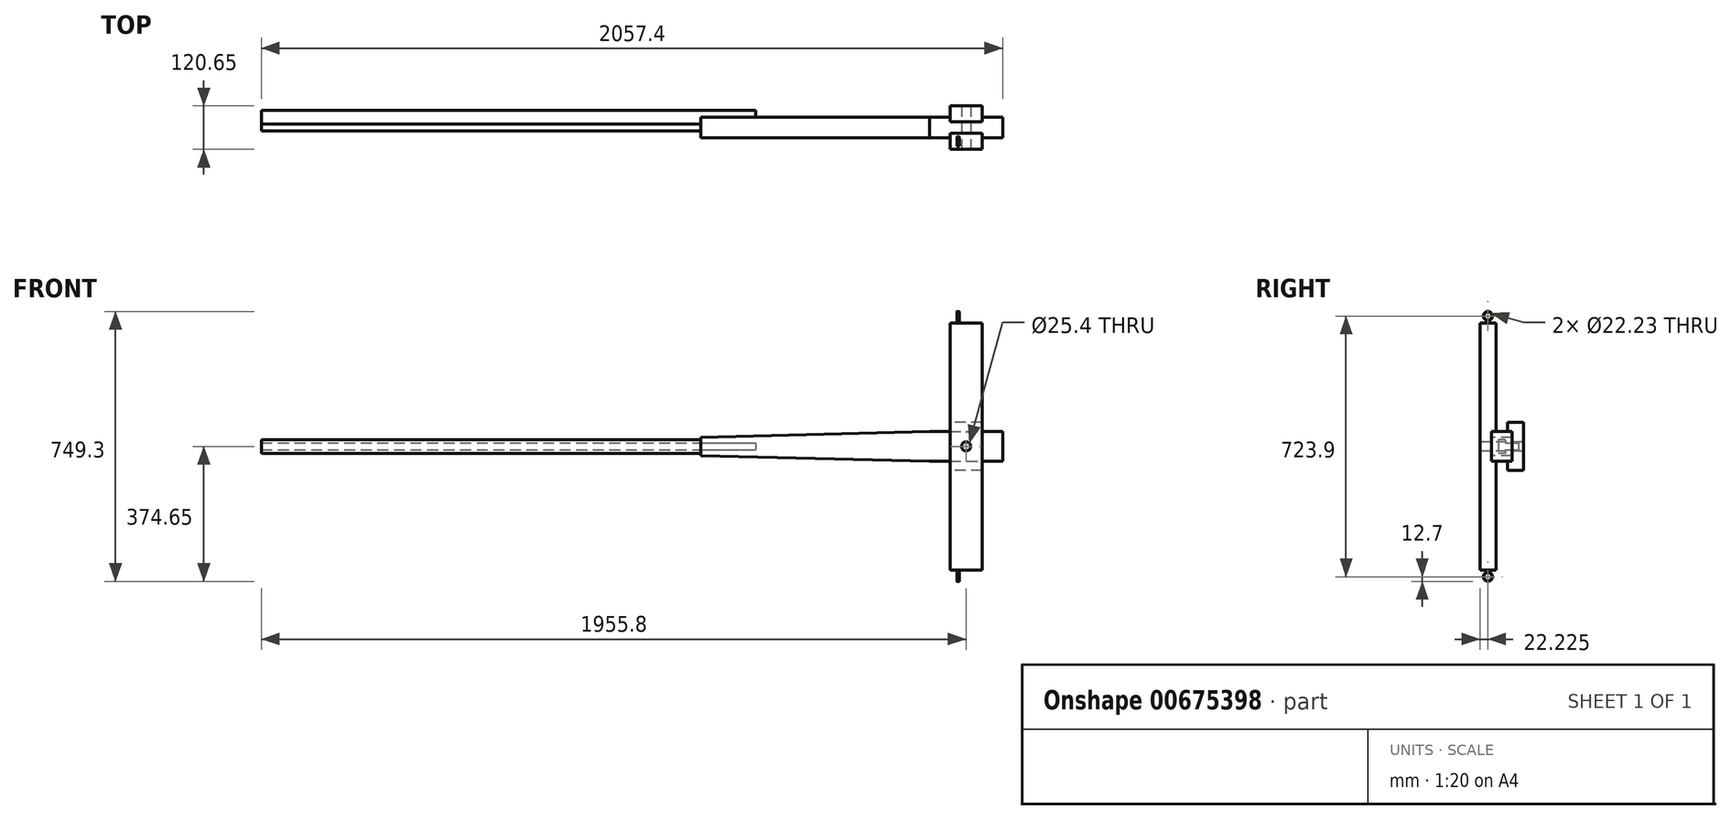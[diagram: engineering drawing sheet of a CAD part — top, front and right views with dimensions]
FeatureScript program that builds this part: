
annotation { "Feature Type Name" : "Feature", "Feature Type Description" : "" }
export const myFeature = defineFeature(function(context is Context, id is Id, definition is map)
    precondition{}
    {
        {
            var Q0;
            Q0=qCreatedBy(makeId("Front.planeOp"),FACE);
            var sketch = newSketch(context, id + "F0", { "sketchPlane" : qUnion([Q0])});
            skLineSegment(sketch, "E0.bottom", {"start": v(101.6, 41.27) * mm, "end": v(-736.6, 41.27) * mm});
            skLineSegment(sketch, "E0.top", {"start": v(101.6, -41.27) * mm, "end": v(-736.6, -41.28) * mm});
            skLineSegment(sketch, "E0.left", {"start": v(101.6, 41.28) * mm, "end": v(101.6, -41.27) * mm});
            skLineSegment(sketch, "E0.right", {"start": v(-736.6, 41.27) * mm, "end": v(-736.6, -41.28) * mm});
            skSolve(sketch);
        }
        {
            var Q0;
            Q0=qSketchRegion(id+"F0",true);
            extrude(context, id + "F1", {"entities" : qUnion([Q0]), "depth" : 57.15 * mm, "offsetDistance" : 25.4 * mm});
        }
        {
            var Q0;
            Q0=makeQuery(id+"F1.opExtrude","CAP_FACE",FACE,{"disambiguationData":[OSD([sQuery(id+"F0.wireOp",EDGE,"E0.bottom"),sQuery(id+"F0.wireOp",EDGE,"E0.top"),sQuery(id+"F0.wireOp",EDGE,"E0.left"),sQuery(id+"F0.wireOp",EDGE,"E0.right")])],"isStart":false});
            var sketch = newSketch(context, id + "F2", { "sketchPlane" : qUnion([Q0])});
            skLineSegment(sketch, "E1", {"start": v(-736.6, 41.27) * mm, "end": v(-736.6, 25.4) * mm});
            skLineSegment(sketch, "E2", {"start": v(-736.6, 25.4) * mm, "end": v(-101.6, 41.27) * mm});
            skLineSegment(sketch, "E3", {"start": v(-101.6, 41.27) * mm, "end": v(-736.6, 41.27) * mm});
            skLineSegment(sketch, "E4", {"start": v(-736.6, -41.28) * mm, "end": v(-736.6, -25.4) * mm});
            skLineSegment(sketch, "E5", {"start": v(-736.6, -25.4) * mm, "end": v(-101.6, -41.27) * mm});
            skLineSegment(sketch, "E6", {"start": v(-101.6, -41.28) * mm, "end": v(-736.6, -41.28) * mm});
            skSolve(sketch);
        }
        {
            var Q0;
            Q0=qSketchRegion(id+"F2",true);
            extrude(context, id + "F3", {"entities" : qUnion([Q0]), "operationType" : NewBodyOperationType.REMOVE, "endBound" : BoundingType.THROUGH_ALL, "oppositeDirection" : true, "depth" : 25.4 * mm, "offsetDistance" : 25.4 * mm});
        }
        {
            var Q0;
            Q0=makeQuery(id+"F1.opExtrude","CAP_FACE",FACE,{"disambiguationData":[OSD([sQuery(id+"F0.wireOp",EDGE,"E0.bottom"),sQuery(id+"F0.wireOp",EDGE,"E0.top"),sQuery(id+"F0.wireOp",EDGE,"E0.left"),sQuery(id+"F0.wireOp",EDGE,"E0.right")])],"isStart":false});
            var sketch = newSketch(context, id + "F4", { "sketchPlane" : qUnion([Q0])});
            skLineSegment(sketch, "E7.left", {"start": v(-44.45, 342.9) * mm, "end": v(-44.45, -342.9) * mm});
            skLineSegment(sketch, "E7.right", {"start": v(44.45, 342.9) * mm, "end": v(44.45, -342.9) * mm});
            skLineSegment(sketch, "E8", {"start": v(-44.45, -342.9) * mm, "end": v(44.45, -342.9) * mm});
            skLineSegment(sketch, "E9", {"start": v(-44.45, 342.9) * mm, "end": v(44.45, 342.9) * mm});
            skSolve(sketch);
        }
        {
            var Q0;
            {var subQ0=sQuery(id+"F4.wireOp",EDGE,"E7.left");var subQ1=makeQuery(id+"F1.opExtrude","CAP_EDGE",EDGE,{"disambiguationData":[OSD([sQuery(id+"F0.wireOp",EDGE,"E0.bottom")])],"isStart":false});var subQ2=makeQuery(id+"F4.imprint","INTERSECT",VERTEX,{"derivedFrom":[subQ1,subQ0]});Q0=makeQuery(id+"F4.imprint","IMPRINT",FACE,{"disambiguationData":[TD([[makeQuery(id+"F4.imprint","IMPRINT",EDGE,{"disambiguationData":[TD([[subQ2,-1.0]])],"derivedFrom":subQ0}),1.0]])]});}
            var Q1;
            {var subQ0=sQuery(id+"F4.wireOp",EDGE,"E9");Q1=makeQuery(id+"F4.imprint","IMPRINT",FACE,{"disambiguationData":[TD([[makeQuery(id+"F4.imprint","IMPRINT",EDGE,{"derivedFrom":subQ0}),-1.0]])]});}
            var Q2;
            {var subQ0=sQuery(id+"F4.wireOp",EDGE,"E8");Q2=makeQuery(id+"F4.imprint","IMPRINT",FACE,{"disambiguationData":[TD([[makeQuery(id+"F4.imprint","IMPRINT",EDGE,{"derivedFrom":subQ0}),1.0]])]});}
            extrude(context, id + "F5", {"entities" : qUnion([Q0, Q1, Q2]), "operationType" : NewBodyOperationType.ADD, "depth" : 31.75 * mm, "offsetDistance" : 25.4 * mm, "hasSecondDirection" : true, "secondDirectionOppositeDirection" : true, "secondDirectionDepth" : 12.7 * mm});
        }
        {
            var Q0;
            Q0=makeQuery(id+"F5.opExtrude","CAP_FACE",FACE,{"disambiguationData":[OSD([sQuery(id+"F4.wireOp",EDGE,"E7.left"),sQuery(id+"F4.wireOp",EDGE,"E7.right"),sQuery(id+"F4.wireOp",EDGE,"c8be6581-7b69-41f4-ac51-68e8a2e033d9.bottom"),sQuery(id+"F4.wireOp",EDGE,"c8be6581-7b69-41f4-ac51-68e8a2e033d9.top"),sQuery(id+"F4.wireOp",EDGE,"c8be6581-7b69-41f4-ac51-68e8a2e033d9.left"),sQuery(id+"F4.wireOp",EDGE,"c8be6581-7b69-41f4-ac51-68e8a2e033d9.right"),sQuery(id+"F4.wireOp",EDGE,"86981ba0-bfa5-46fc-8650-502ccc05c84c.bottom"),sQuery(id+"F4.wireOp",EDGE,"86981ba0-bfa5-46fc-8650-502ccc05c84c.top"),sQuery(id+"F4.wireOp",EDGE,"86981ba0-bfa5-46fc-8650-502ccc05c84c.left"),sQuery(id+"F4.wireOp",EDGE,"86981ba0-bfa5-46fc-8650-502ccc05c84c.right")])],"isStart":false});
            var sketch = newSketch(context, id + "F6", { "sketchPlane" : qUnion([Q0])});
            skCircle(sketch, "E10", {"center": v(0, 0) * mm, "radius": 12.7 * mm});
            skSolve(sketch);
        }
        {
            var Q0;
            Q0=qSketchRegion(id+"F6",true);
            extrude(context, id + "F7", {"entities" : qUnion([Q0]), "operationType" : NewBodyOperationType.REMOVE, "endBound" : BoundingType.THROUGH_ALL, "oppositeDirection" : true, "depth" : 25.4 * mm, "offsetDistance" : 25.4 * mm});
        }
        {
            var Q0;
            Q0=makeQuery(id+"F1.opExtrude","SWEPT_FACE",FACE,{"disambiguationData":[OSD([sQuery(id+"F0.wireOp",EDGE,"E0.right")])]});
            var sketch = newSketch(context, id + "F8", { "sketchPlane" : qUnion([Q0])});
            skLineSegment(sketch, "E11.bottom", {"start": v(19.05, 19.05) * mm, "end": v(38.1, 19.05) * mm});
            skLineSegment(sketch, "E11.top", {"start": v(19.05, -19.05) * mm, "end": v(38.1, -19.05) * mm});
            skLineSegment(sketch, "E11.left", {"start": v(19.05, 19.05) * mm, "end": v(19.05, -19.05) * mm});
            skLineSegment(sketch, "E11.right", {"start": v(38.1, 19.05) * mm, "end": v(38.1, -19.05) * mm});
            skLineSegment(sketch, "E12.left", {"start": v(38.1, 19.05) * mm, "end": v(38.1, 0) * mm});
            skLineSegment(sketch, "E13.left", {"start": v(19.05, -19.05) * mm, "end": v(19.05, 0) * mm});
            skLineSegment(sketch, "E14.bottom", {"start": v(19.05, -9.52) * mm, "end": v(-19.05, -9.52) * mm});
            skLineSegment(sketch, "E14.top", {"start": v(19.05, 9.53) * mm, "end": v(-19.05, 9.53) * mm});
            skLineSegment(sketch, "E14.left", {"start": v(19.05, -9.52) * mm, "end": v(19.05, 9.53) * mm});
            skLineSegment(sketch, "E14.right", {"start": v(-19.05, -9.52) * mm, "end": v(-19.05, 9.53) * mm});
            skSolve(sketch);
        }
        {
            var Q0;
            Q0=qSketchRegion(id+"F8",true);
            extrude(context, id + "F9", {"entities" : qUnion([Q0]), "operationType" : NewBodyOperationType.ADD, "depth" : 1219.2 * mm, "offsetDistance" : 25.4 * mm, "hasSecondDirection" : true, "secondDirectionOppositeDirection" : true, "secondDirectionDepth" : 152.4 * mm});
        }
        {
            var Q0;
            Q0=makeQuery(id+"F1.opExtrude","CAP_FACE",FACE,{"disambiguationData":[OSD([sQuery(id+"F0.wireOp",EDGE,"E0.bottom"),sQuery(id+"F0.wireOp",EDGE,"E0.top"),sQuery(id+"F0.wireOp",EDGE,"E0.left"),sQuery(id+"F0.wireOp",EDGE,"E0.right")])],"isStart":true});
            var sketch = newSketch(context, id + "F10", { "sketchPlane" : qUnion([Q0])});
            skLineSegment(sketch, "E15.bottom", {"start": v(-44.45, 66.67) * mm, "end": v(44.45, 66.67) * mm});
            skLineSegment(sketch, "E15.top", {"start": v(-44.45, -66.68) * mm, "end": v(44.45, -66.68) * mm});
            skLineSegment(sketch, "E15.left", {"start": v(-44.45, 66.67) * mm, "end": v(-44.45, -66.68) * mm});
            skLineSegment(sketch, "E15.right", {"start": v(44.45, 66.67) * mm, "end": v(44.45, -66.68) * mm});
            skSolve(sketch);
        }
        {
            var Q0;
            Q0 = qSketchRegion(id + "F10", true);
            extrude(context, id + "F11", {"entities" : qUnion([Q0]), "operationType" : NewBodyOperationType.ADD, "depth" : 31.75 * mm, "offsetDistance" : 25.4 * mm, "hasSecondDirection" : true, "secondDirectionOppositeDirection" : true, "secondDirectionDepth" : 12.7 * mm});
        }
        {
            var Q0;
            Q0=makeQuery(id+"F11.opExtrude","CAP_FACE",FACE,{"disambiguationData":[OSD([sQuery(id+"F10.wireOp",EDGE,"E15.bottom"),sQuery(id+"F10.wireOp",EDGE,"E15.top"),sQuery(id+"F10.wireOp",EDGE,"E15.left"),sQuery(id+"F10.wireOp",EDGE,"E15.right")])],"isStart":false});
            var sketch = newSketch(context, id + "F12", { "sketchPlane" : qUnion([Q0])});
            skCircle(sketch, "E16", {"center": v(0, 0) * mm, "radius": 12.7 * mm});
            skSolve(sketch);
        }
        {
            var Q0;
            Q0 = qSketchRegion(id + "F12", true);
            extrude(context, id + "F13", {"entities" : qUnion([Q0]), "operationType" : NewBodyOperationType.REMOVE, "endBound" : BoundingType.THROUGH_ALL, "oppositeDirection" : true, "depth" : 25.4 * mm, "offsetDistance" : 25.4 * mm});
        }
        {
            var Q0;
            Q0=makeQuery(id+"F5.opExtrude","SWEPT_FACE",FACE,{"disambiguationData":[OSD([sQuery(id+"F4.wireOp",EDGE,"E7.left")])]});
            var sketch = newSketch(context, id + "F14", { "sketchPlane" : qUnion([Q0])});
            skCircle(sketch, "E17", {"center": v(66.68, 361.95) * mm, "radius": 11.11 * mm});
            skArc(sketch, "E18", {"start": v(69.85, 349.65) * mm, "mid": v(66.67, 374.65) * mm, "end": v(63.5, 349.65) * mm});
            skLineSegment(sketch, "E19.top", {"start": v(63.5, 323.85) * mm, "end": v(69.85, 323.85) * mm});
            skLineSegment(sketch, "E19.left", {"start": v(63.5, 349.65) * mm, "end": v(63.5, 323.85) * mm});
            skLineSegment(sketch, "E19.right", {"start": v(69.85, 349.65) * mm, "end": v(69.85, 323.85) * mm});
            skSolve(sketch);
        }
        {
            var Q0;
            Q0 = qSketchRegion(id + "F14", true);
            extrude(context, id + "F15", {"entities" : qUnion([Q0]), "operationType" : NewBodyOperationType.ADD, "oppositeDirection" : true, "depth" : 25.4 * mm, "offsetDistance" : 25.4 * mm, "hasSecondDirection" : true, "secondDirectionOppositeDirection" : true, "secondDirectionDepth" : 19.05 * mm});
        }
        {
            var Q0;
            Q0=makeQuery(id+"F15.opExtrude","CAP_EDGE",EDGE,{"disambiguationData":[OSD([sQuery(id+"F14.wireOp",EDGE,"E19.right")])],"isStart":true});
            var Q1;
            Q1=makeQuery(id+"F15.opExtrude","CAP_EDGE",EDGE,{"disambiguationData":[OSD([sQuery(id+"F14.wireOp",EDGE,"E19.left")])],"isStart":true});
            var Q2;
            Q2=makeQuery(id+"F15.opExtrude","CAP_EDGE",EDGE,{"disambiguationData":[OSD([sQuery(id+"F14.wireOp",EDGE,"E19.right")])],"isStart":false});
            var Q3;
            Q3=makeQuery(id+"F15.opExtrude","CAP_EDGE",EDGE,{"disambiguationData":[OSD([sQuery(id+"F14.wireOp",EDGE,"E19.left")])],"isStart":false});
            fillet(context, id + "F16", {"entities" : qUnion([Q0, Q1, Q2, Q3]), "radius" : 3.17 * mm, "tangentPropagation" : true, "allowEdgeOverflow" : false});
        }
        {
            var Q0;
            Q0=makeQuery(id+"F15.opExtrude","CAP_EDGE",EDGE,{"disambiguationData":[OSD([sQuery(id+"F14.wireOp",EDGE,"E17")])],"isStart":true});
            var Q1;
            Q1=makeQuery(id+"F15.opExtrude","CAP_EDGE",EDGE,{"disambiguationData":[OSD([sQuery(id+"F14.wireOp",EDGE,"E18")])],"isStart":true});
            var Q2;
            Q2=makeQuery(id+"F15.opExtrude","CAP_EDGE",EDGE,{"disambiguationData":[OSD([sQuery(id+"F14.wireOp",EDGE,"E17")])],"isStart":false});
            var Q3;
            Q3=makeQuery(id+"F15.opExtrude","CAP_EDGE",EDGE,{"disambiguationData":[OSD([sQuery(id+"F14.wireOp",EDGE,"E18")])],"isStart":false});
            fillet(context, id + "F17", {"entities" : qUnion([Q0, Q1, Q2, Q3]), "radius" : 0.64 * mm, "tangentPropagation" : true, "allowEdgeOverflow" : false});
        }
        {
            var Q0;
            Q0=makeQuery(id+"F5.opExtrude","SWEPT_FACE",FACE,{"disambiguationData":[OSD([sQuery(id+"F4.wireOp",EDGE,"E7.left")])]});
            var sketch = newSketch(context, id + "F18", { "sketchPlane" : qUnion([Q0])});
            skArc(sketch, "E20.MirrorCS", {"start": v(69.85, -349.65) * mm, "mid": v(66.67, -374.65) * mm, "end": v(63.5, -349.65) * mm});
            skLineSegment(sketch, "E21.MirrorCS", {"start": v(63.5, -323.85) * mm, "end": v(69.85, -323.85) * mm});
            skLineSegment(sketch, "E22.MirrorCS", {"start": v(63.5, -349.65) * mm, "end": v(63.5, -323.85) * mm});
            skLineSegment(sketch, "E23.MirrorCS", {"start": v(69.85, -349.65) * mm, "end": v(69.85, -323.85) * mm});
            skCircle(sketch, "E24.MirrorC", {"center": v(66.68, -361.95) * mm, "radius": 11.11 * mm});
            skSolve(sketch);
        }
        {
            var Q0;
            Q0 = qSketchRegion(id + "F18", true);
            extrude(context, id + "F19", {"entities" : qUnion([Q0]), "operationType" : NewBodyOperationType.ADD, "oppositeDirection" : true, "depth" : 25.4 * mm, "offsetDistance" : 25.4 * mm, "hasSecondDirection" : true, "secondDirectionOppositeDirection" : true, "secondDirectionDepth" : 19.05 * mm});
        }
        {
            var Q0;
            Q0=makeQuery(id+"F19.opExtrude","CAP_EDGE",EDGE,{"disambiguationData":[OSD([sQuery(id+"F18.wireOp",EDGE,"E23.MirrorCS")])],"isStart":true});
            var Q1;
            Q1=makeQuery(id+"F19.opExtrude","CAP_EDGE",EDGE,{"disambiguationData":[OSD([sQuery(id+"F18.wireOp",EDGE,"E22.MirrorCS")])],"isStart":true});
            var Q2;
            Q2=makeQuery(id+"F19.opExtrude","CAP_EDGE",EDGE,{"disambiguationData":[OSD([sQuery(id+"F18.wireOp",EDGE,"E23.MirrorCS")])],"isStart":false});
            var Q3;
            Q3=makeQuery(id+"F19.opExtrude","CAP_EDGE",EDGE,{"disambiguationData":[OSD([sQuery(id+"F18.wireOp",EDGE,"E22.MirrorCS")])],"isStart":false});
            fillet(context, id + "F20", {"entities" : qUnion([Q0, Q1, Q2, Q3]), "radius" : 3.17 * mm, "tangentPropagation" : true, "allowEdgeOverflow" : false});
        }
        {
            var Q0;
            Q0=makeQuery(id+"F19.opExtrude","CAP_EDGE",EDGE,{"disambiguationData":[OSD([sQuery(id+"F18.wireOp",EDGE,"E20.MirrorCS")])],"isStart":false});
            var Q1;
            Q1=makeQuery(id+"F19.opExtrude","CAP_EDGE",EDGE,{"disambiguationData":[OSD([sQuery(id+"F18.wireOp",EDGE,"E24.MirrorC")])],"isStart":false});
            var Q2;
            Q2=makeQuery(id+"F19.opExtrude","CAP_EDGE",EDGE,{"disambiguationData":[OSD([sQuery(id+"F18.wireOp",EDGE,"E24.MirrorC")])],"isStart":true});
            var Q3;
            Q3=makeQuery(id+"F19.opExtrude","CAP_EDGE",EDGE,{"disambiguationData":[OSD([sQuery(id+"F18.wireOp",EDGE,"E20.MirrorCS")])],"isStart":true});
            fillet(context, id + "F21", {"entities" : qUnion([Q0, Q1, Q2, Q3]), "radius" : 0.64 * mm, "tangentPropagation" : true, "allowEdgeOverflow" : false});
        }
    });
